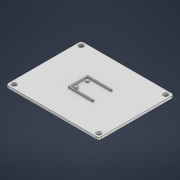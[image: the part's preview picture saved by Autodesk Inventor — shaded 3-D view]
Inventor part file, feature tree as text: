
AUTODESK INVENTOR PART (.ipt)
format: ipt  version: 2022 (Build 260153000, 153)  size: 172,032 bytes
history: native  units: mm
features: extrude x5, sketch x4, other x1, chamfer x1, fillet x1
ambient origin geometry x8: Origin, YZ Plane, XZ Plane, XY Plane, X Axis, Y Axis, Z Axis, Center Point
bodies: Body1 (feature_tree)
feature tree (12):
  other  "Těleso1"
  extrude  "Vysunutí1"  Depth=2.0mm
  extrude  "Vysunutí2"  Depth=2.0mm
  chamfer  "Zkosení1"  Distance=2.0mm
  fillet  "Zaoblení1"  Radius=2.0mm
  sketch  "Náčrt3"
  extrude  "Vysunutí3"  Depth=75.0mm
  extrude  "Vysunutí4"  Depth=60.0mm
  extrude  "Vysunutí5"  Depth=2.0mm TaperAngle=0.0deg
  sketch  "Náčrt1"
  sketch  "Náčrt2"
  sketch  "Náčrt4"
